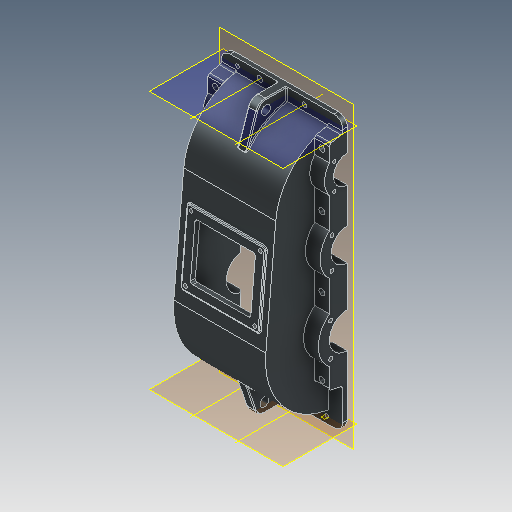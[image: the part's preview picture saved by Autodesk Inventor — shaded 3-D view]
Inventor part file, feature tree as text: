
AUTODESK INVENTOR PART (.ipt)
format: ipt  version: 2025 (Build 290162000, 162)  size: 675,840 bytes
history: native  units: mm
features: reference x41, other x28, sketch x13, extrude x7, hole x5, thread x5, plane x4, fillet x2, revolve x2, shell x1, mirror x1, chamfer x1, projected_geometry x1
ambient origin geometry x8: Origin, YZ Plane, XZ Plane, XY Plane, X Axis, Y Axis, Z Axis, Center Point
bodies: 实体1 (feature_tree)
feature tree (111):
  plane  "工作平面1"
  extrude  "拉伸1"  Depth=10.0mm
  extrude  "拉伸2"  Depth=80.0mm
  shell  "抽壳1"  Thickness=206.0mm
  extrude  "拉伸3"  Depth=8.0mm
  extrude  "拉伸4"  Depth=40.0mm
  mirror  "镜像1"
  hole  "孔1"  [1 undecoded]
  hole  "孔3"  [1 undecoded]
  hole  "孔4"  [1 undecoded]
  hole  "孔5"  [1 undecoded]
  hole  "孔6"  [1 undecoded]
  sketch  "草图13"  dims[d46=28.0mm d47=4.0mm d48=2.0mm d49=90.0deg d50=30.0mm d51=120.0deg]
  extrude  "拉伸5"  Depth=8.0mm
  extrude  "拉伸6"  Depth=8.0mm
  fillet  "圆角2"  Radius=120.0mm
  thread  "螺纹1"  [1 undecoded]
  thread  "螺纹2"  [1 undecoded]
  thread  "螺纹3"  [1 undecoded]
  thread  "螺纹4"  [1 undecoded]
  extrude  "拉伸7"  Depth=8.0mm TaperAngle=0.0deg
  fillet  "圆角3"  Radius=20.0mm
  plane  "工作平面2"
  revolve  "旋转1"  [1 undecoded]
  plane  "工作平面3"
  plane  "工作平面4"
  revolve  "旋转2"  [1 undecoded]
  thread  "螺纹5"  [1 undecoded]
  chamfer  "倒角1"  Distance=20.0mm
  sketch  "草图1"  dims[d0=10.0mm d1=0.0mm d2=300.0mm]
  reference  "参考1"
  reference  "参考2"
  reference  "参考3"
  reference  "参考4"
  reference  "参考5"
  reference  "参考6"
  sketch  "草图2"  dims[d3=270.0mm d4=80.0mm d5=206.0mm d6=0.0mm]
  reference  "参考7"
  reference  "参考8"
  reference  "参考9"
  sketch  "草图3"  dims[d7=8.0mm d8=8.0mm]
  reference  "参考11"
  reference  "参考12"
  reference  "参考13"
  sketch  "草图4"  dims[d9=0.0mm d10=0.0mm d11=40.0mm]
  projected_geometry  "投影回路1"
  reference  "参考14"
  reference  "参考15"
  reference  "参考16"
  reference  "参考17"
  reference  "参考18"
  sketch  "草图5"  dims[d12=29.408798mm d13=29.408798mm]
  reference  "参考19"
  reference  "参考20"
  reference  "参考21"
  reference  "参考22"
  reference  "参考23"
  reference  "参考24"
  reference  "参考25"
  reference  "参考26"
  sketch  "草图9"  dims[d14=36.0mm d15=0.0mm d16=5.0mm]
  reference  "参考33"
  reference  "参考34"
  sketch  "草图10"  dims[d17=13.0mm d18=6.0mm d19=4.0mm d20=2.0mm d21=90.0deg d22=8.0mm d23=20.594885mm]
  reference  "参考35"
  reference  "参考36"
  sketch  "草图11"  dims[d32=28.0mm d33=4.0mm d34=2.0mm d35=90.0deg d36=30.0mm d37=120.0deg]
  reference  "参考37"
  reference  "参考38"
  reference  "参考39"
  reference  "参考40"
  sketch  "草图12"  dims[d39=28.0mm d40=4.0mm d41=2.0mm d42=90.0deg d43=30.0mm d44=120.0deg]
  reference  "参考41"
  reference  "参考42"
  reference  "参考43"
  reference  "参考44"
  sketch  "草图14"  dims[d53=28.0mm d54=4.0mm d55=2.0mm d56=90.0deg d57=30.0mm d58=120.0deg d59=175.0mm]
  other  "工作轴1"
  other  "工作轴2"
  sketch  "草图15"  dims[d60=160.0mm d61=5.0mm]
  reference  "参考45"
  reference  "参考46"
  other  "工作轴3"
  other  "工作轴4"
  sketch  "草图16"  dims[d62=155.0mm d63=140.0mm d64=8.0mm d65=135.0mm d66=120.0mm d67=5.0mm d68=3.0mm d69=0.0mm d70=3.0mm d71=0.0mm d72=2.0mm d73=11.0mm d74=0.0mm d75=20.0mm d76=0.0mm d77=11.0mm d78=0.0mm d79=20.0mm d80=0.0mm d81=22.0mm d82=20.0mm d83=142.282327mm d84=162.282327mm d85=90.0mm d86=20.0mm d87=0.0mm d88=2.0mm d91=166.895756mm d92=90.0mm d93=22.0mm d94=186.895756mm d95=20.0mm d96=28.0mm d97=28.0mm d98=90.0deg d99=90.0deg d100=10.0mm d101=10.0mm d102=0.0mm d103=8.0mm d104=2.0mm d105=45.0deg]
  reference  "参考47"
  reference  "参考48"
  other  "齿轮箱.iam"
  other  "下半箱体:1"
  other  "低速齿轮:1"
  other  "正齿轮:1"
  other  "正齿轮2:1"
  other  "高速齿轮:1"
  other  "高速轴:1"
  other  "轴承:2"
  other  "滚动轴承 GB/T 276-1994 60000 和 160000 型 6206:1"
  other  "中间轴:1"
  other  "滚动轴承 GB/T 276-1994 60000 和 160000 型 6306:1"
  other  "低速轴:1"
  other  "滚动轴承 GB/T 276-1994 60000 和 160000 型 6010:1"
  other  "高速轴承透盖"
  other  "高速轴承闷盖"
  other  "中间轴承闷盖1"
  other  "低速轴承透盖"
  other  "中间轴承闷盖2"
  other  "低速轴承闷盖"
  other  "定位销:1"
  other  "定位销:2"
  parser-record x1  (decoder bookkeeping rows leaked as tree rows — omitted from the tree; the rows remain in map.json)
  other  "齿轮箱1.iam"
  other  "<userpath>\Desktop\Inventor files\齿轮箱.iam"
note: 12 required parameter values undecoded (feature->parameter linkage not recoverable at this tier; creation-order binding heuristic only, values carry confidence <= 0.55)
note: 1 file-system path scrubbed to <path> (originals preserved in map.json)